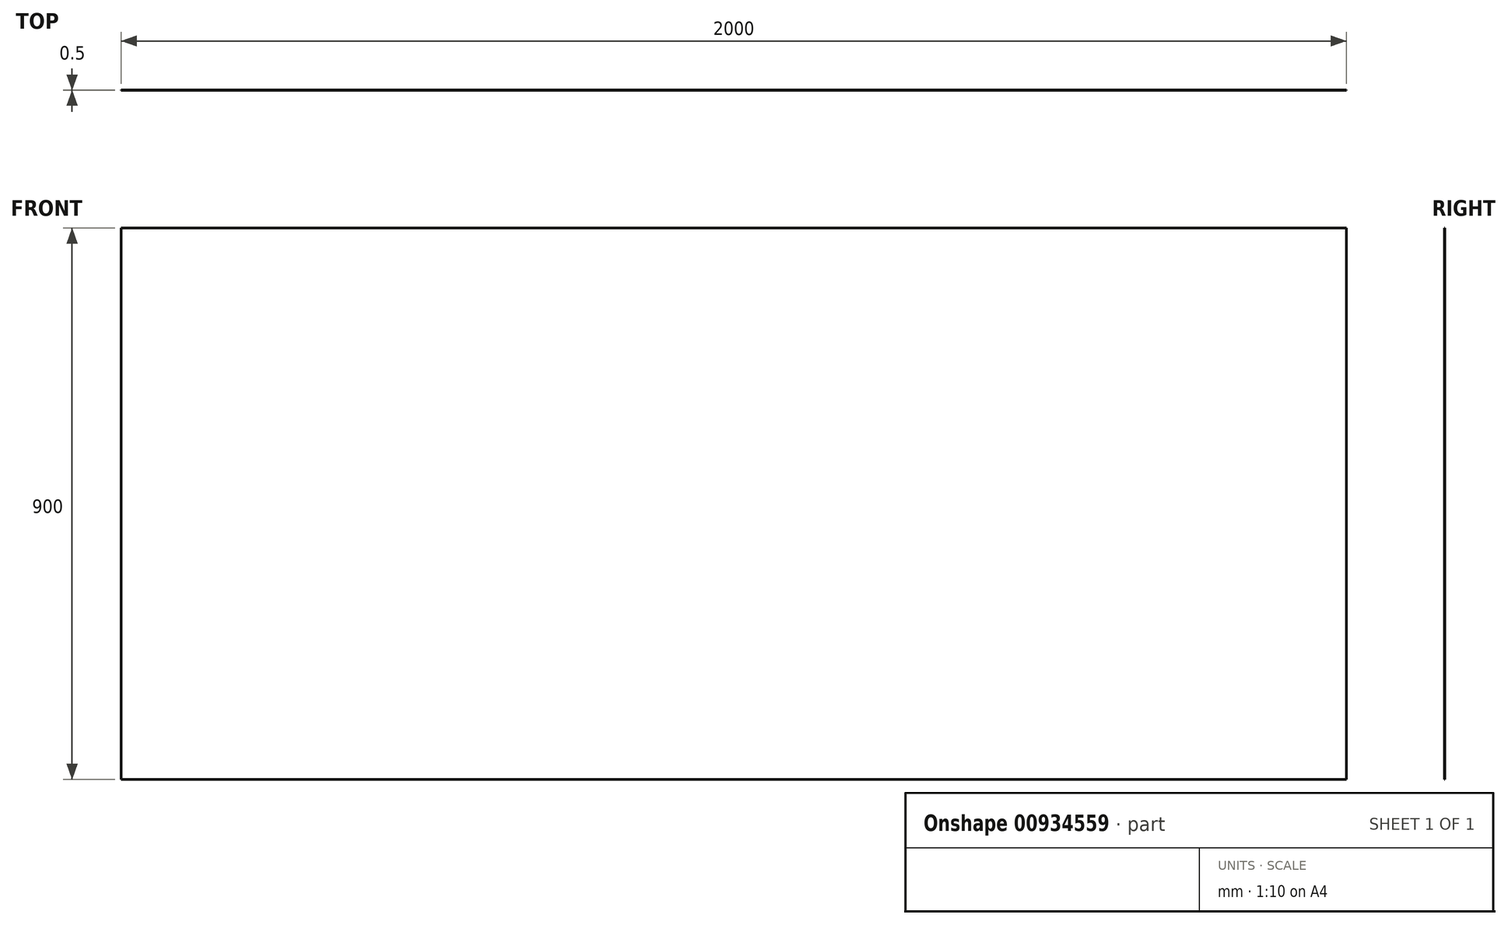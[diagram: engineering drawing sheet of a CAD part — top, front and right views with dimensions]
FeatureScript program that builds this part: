
annotation { "Feature Type Name" : "Feature", "Feature Type Description" : "" }
export const myFeature = defineFeature(function(context is Context, id is Id, definition is map)
    precondition{}
    {
        {
            var Q0;
            Q0=qCreatedBy(makeId("Front.planeOp"),FACE);
            var sketch = newSketch(context, id + "F0", { "sketchPlane" : qUnion([Q0])});
            skLineSegment(sketch, "E0.bottom", {"start": v(1000, 450) * mm, "end": v(-1000, 450) * mm});
            skLineSegment(sketch, "E0.top", {"start": v(1000, -450) * mm, "end": v(-1000, -450) * mm});
            skLineSegment(sketch, "E0.left", {"start": v(1000, 450) * mm, "end": v(1000, -450) * mm});
            skLineSegment(sketch, "E0.right", {"start": v(-1000, 450) * mm, "end": v(-1000, -450) * mm});
            skPoint(sketch, "E0.middle", {"position": v(0, 0) * mm});
            skSolve(sketch);
        }
        {
            var Q0;
            Q0=makeQuery(id+"F0.imprint","IMPRINT",FACE,{"disambiguationData":[TD([[makeQuery(id+"F0.imprint","IMPRINT",EDGE,{"derivedFrom":sQuery(id+"F0.wireOp",EDGE,"E0.bottom")}),1.0]])]});
            extrude(context, id + "F1", {"entities" : qUnion([Q0]), "depth" : 0.5 * mm, "offsetDistance" : 25 * mm});
        }
    });
